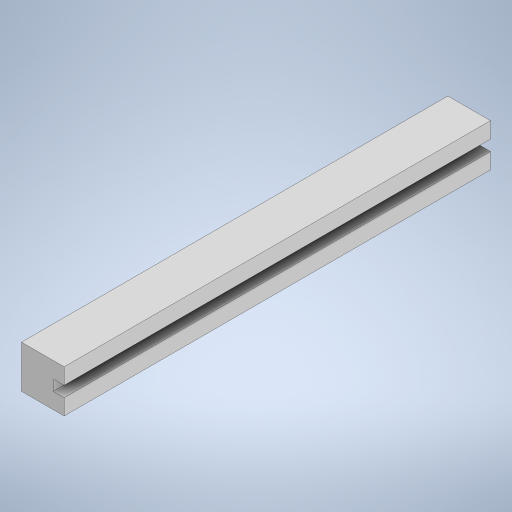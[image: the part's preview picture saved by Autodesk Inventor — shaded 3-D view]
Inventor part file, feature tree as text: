
AUTODESK INVENTOR PART (.ipt)
format: ipt  version: 2023 (Build 270158000, 158)  size: 254,464 bytes
history: native  units: in
note: dims shown in document units (in); Inventor stores cm internally (conversion verified against a paired STEP export)
features: extrude x3, sketch x3, chamfer x1
ambient origin geometry x8: Origin, YZ Plane, XZ Plane, XY Plane, X Axis, Y Axis, Z Axis, Center Point
bodies: Solid1 (feature_tree)
feature tree (7):
  extrude  "Extrusion1"  Depth=10.0in
  extrude  "Extrusion2"  Depth=0.25in
  extrude  "Extrusion3"  Depth=0.25in TaperAngle=0.0deg
  chamfer  "Chamfer1"  Distance=0.125in
  sketch  "Sketch1"  dims[d0=1.0in d1=10.0in]
  sketch  "Sketch2"  dims[d2=1.0in d3=0.0in d4=0.25in]
  sketch  "Sketch3"  dims[d5=0.375in d6=0.25in d7=0.0in d8=0.125in d9=0.125in d10=0.5in d11=0.5in d12=0.5in d13=0.5in d14=3.0in d15=0.0in d16=0.125in d17=0.125in d18=45.0deg]
